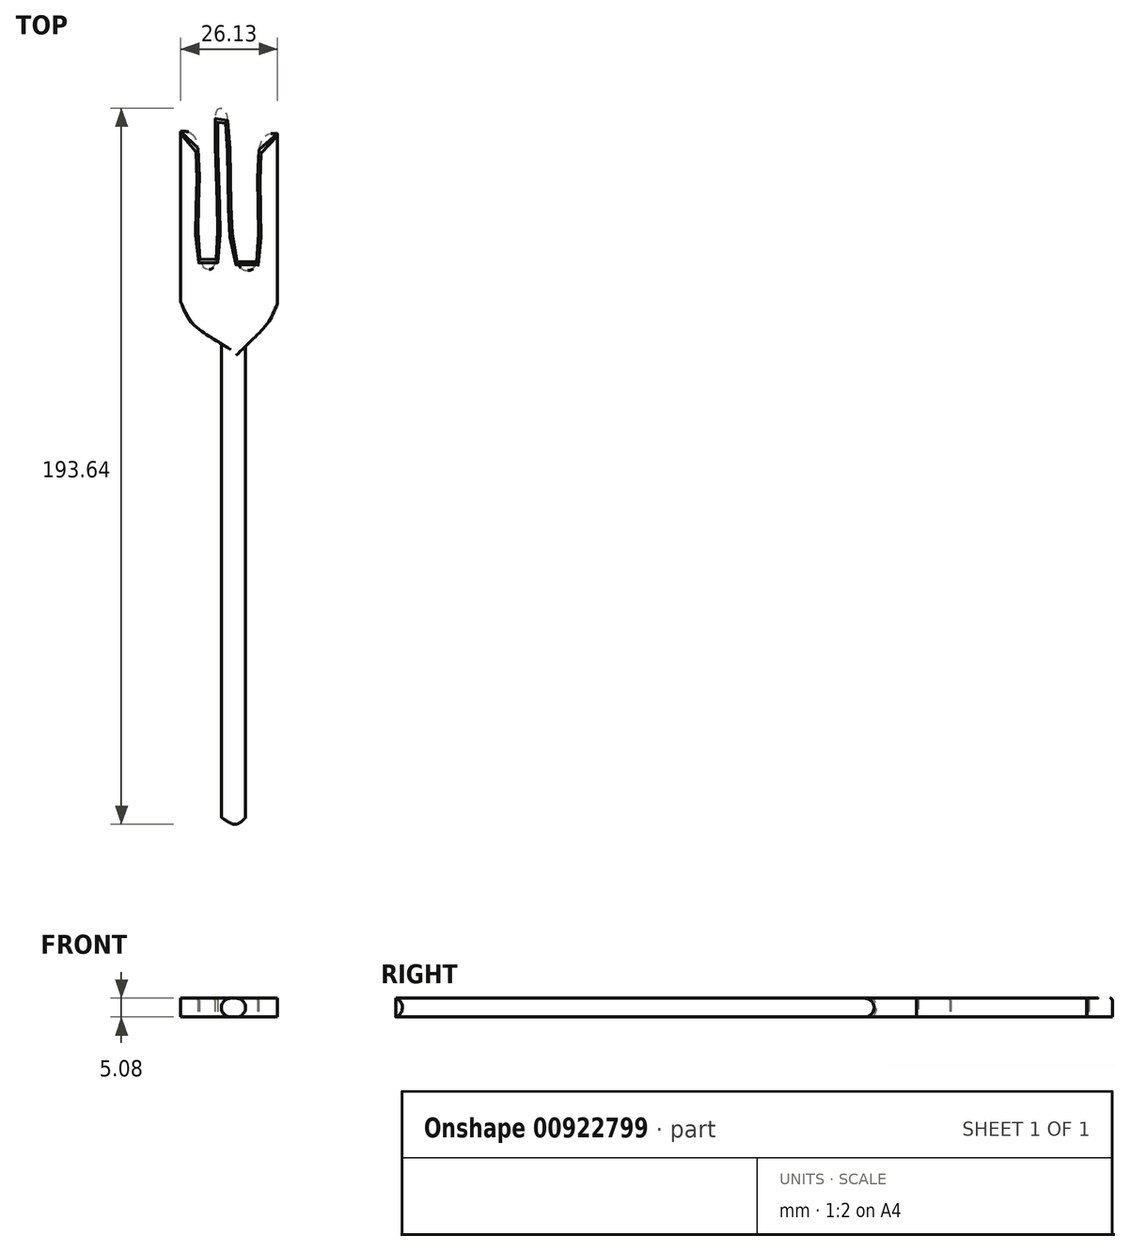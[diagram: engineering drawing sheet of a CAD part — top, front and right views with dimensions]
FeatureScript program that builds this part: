
annotation { "Feature Type Name" : "Feature", "Feature Type Description" : "" }
export const myFeature = defineFeature(function(context is Context, id is Id, definition is map)
    precondition{}
    {
        {
            var Q0;
            Q0=qCreatedBy(makeId("Top.planeOp"),FACE);
            var sketch = newSketch(context, id + "F0", { "sketchPlane" : qUnion([Q0])});
            skLineSegment(sketch, "E0", {"start": v(-28.75, 39.47) * mm, "end": v(-28.75, -87.53) * mm});
            skLineSegment(sketch, "E1", {"start": v(-17.13, 39.73) * mm, "end": v(-17.13, -87.27) * mm});
            skFitSpline(sketch, "E2", {"points": [v(-28.75, -87.53) * mm, v(-24.05, -91.53) * mm, v(-17.13, -87.27) * mm], "startDerivative": vector(9.45, -12.43) * mm, "endDerivative": vector(23.62, 29.9) * mm});
            skLineSegment(sketch, "E3", {"start": v(-37.2, 95.37) * mm, "end": v(-37.2, 49.28) * mm});
            skLineSegment(sketch, "E4", {"start": v(-11.06, 94.71) * mm, "end": v(-11.06, 48.78) * mm});
            skFitSpline(sketch, "E5", {"points": [v(-37.2, 49.28) * mm, v(-34.12, 43.55) * mm, v(-28.75, 39.47) * mm], "startDerivative": vector(5.1, -12.43) * mm, "endDerivative": vector(11.75, -7.22) * mm});
            skFitSpline(sketch, "E6", {"points": [v(-11.06, 48.78) * mm, v(-13.4, 43.91) * mm, v(-17.13, 39.73) * mm], "startDerivative": vector(-4.07, -10.2) * mm, "endDerivative": vector(-8.06, -7.9) * mm});
            skFitSpline(sketch, "E7", {"points": [v(-37.2, 95.37) * mm, v(-33.17, 93.3) * mm, v(-32.05, 61.08) * mm, v(-29.55, 58.02) * mm, v(-27.6, 60.52) * mm, v(-27.6, 100.25) * mm, v(-26.5, 101.64) * mm, v(-24.83, 99.97) * mm, v(-22.05, 60.24) * mm, v(-18.72, 57.74) * mm, v(-16.5, 60.52) * mm, v(-15.59, 92.05) * mm, v(-11.06, 94.71) * mm], "startDerivative": vector(87.16, -0.3) * mm, "endDerivative": vector(113.72, -13.53) * mm});
            skSolve(sketch);
        }
        {
            var Q0;
            Q0=makeQuery(id+"F0.imprint","IMPRINT",FACE,{"disambiguationData":[TD([[makeQuery(id+"F0.imprint","IMPRINT",EDGE,{"derivedFrom":sQuery(id+"F0.wireOp",EDGE,"E0")}),1.0]])]});
            extrude(context, id + "F1", {"entities" : qUnion([Q0]), "depth" : 5.08 * mm, "offsetDistance" : 25.4 * mm});
        }
        {
            var Q0;
            Q0=makeQuery(id+"F1.opExtrude","CAP_EDGE",EDGE,{"disambiguationData":[OSD([sQuery(id+"F0.wireOp",EDGE,"E7")])],"isStart":false});
            fillet(context, id + "F2", {"entities" : qUnion([Q0]), "radius" : 0.61 * mm, "tangentPropagation" : true, "allowEdgeOverflow" : false});
        }
        {
            var Q0;
            Q0=makeQuery(id+"F1.opExtrude","CAP_EDGE",EDGE,{"disambiguationData":[OSD([sQuery(id+"F0.wireOp",EDGE,"E0")])],"isStart":false});
            var Q1;
            Q1=makeQuery(id+"F1.opExtrude","CAP_EDGE",EDGE,{"disambiguationData":[OSD([sQuery(id+"F0.wireOp",EDGE,"E1")])],"isStart":false});
            fillet(context, id + "F3", {"entities" : qUnion([Q0, Q1]), "radius" : 5.08 * mm, "tangentPropagation" : true, "allowEdgeOverflow" : false});
        }
        {
            var Q0;
            {var subQ0=sQuery(id+"F0.wireOp",EDGE,"E1");Q0=makeQuery(id+"F3.opFillet","BLEND_EDGE",EDGE,{"blendedFrom":[makeQuery(id+"F1.opExtrude","CAP_EDGE",EDGE,{"disambiguationData":[OSD([subQ0])],"isStart":false}),makeQuery(id+"F1.opExtrude","CAP_FACE",FACE,{"disambiguationData":[OSD([sQuery(id+"F0.wireOp",EDGE,"E0"),subQ0,sQuery(id+"F0.wireOp",EDGE,"E2"),sQuery(id+"F0.wireOp",EDGE,"E3"),sQuery(id+"F0.wireOp",EDGE,"E4"),sQuery(id+"F0.wireOp",EDGE,"E5"),sQuery(id+"F0.wireOp",EDGE,"E6"),sQuery(id+"F0.wireOp",EDGE,"E7")])],"isStart":true})],"blendedInto":[makeQuery(id+"F1.opExtrude","CAP_FACE",FACE,{"disambiguationData":[OSD([sQuery(id+"F0.wireOp",EDGE,"E0"),subQ0,sQuery(id+"F0.wireOp",EDGE,"E2"),sQuery(id+"F0.wireOp",EDGE,"E3"),sQuery(id+"F0.wireOp",EDGE,"E4"),sQuery(id+"F0.wireOp",EDGE,"E5"),sQuery(id+"F0.wireOp",EDGE,"E6"),sQuery(id+"F0.wireOp",EDGE,"E7")])],"isStart":true})]});}
            var Q1;
            {var subQ0=sQuery(id+"F0.wireOp",EDGE,"E0");Q1=makeQuery(id+"F3.opFillet","BLEND_EDGE",EDGE,{"blendedFrom":[makeQuery(id+"F1.opExtrude","CAP_EDGE",EDGE,{"disambiguationData":[OSD([subQ0])],"isStart":false}),makeQuery(id+"F1.opExtrude","CAP_FACE",FACE,{"disambiguationData":[OSD([subQ0,sQuery(id+"F0.wireOp",EDGE,"E1"),sQuery(id+"F0.wireOp",EDGE,"E2"),sQuery(id+"F0.wireOp",EDGE,"E3"),sQuery(id+"F0.wireOp",EDGE,"E4"),sQuery(id+"F0.wireOp",EDGE,"E5"),sQuery(id+"F0.wireOp",EDGE,"E6"),sQuery(id+"F0.wireOp",EDGE,"E7")])],"isStart":true})],"blendedInto":[makeQuery(id+"F1.opExtrude","CAP_FACE",FACE,{"disambiguationData":[OSD([subQ0,sQuery(id+"F0.wireOp",EDGE,"E1"),sQuery(id+"F0.wireOp",EDGE,"E2"),sQuery(id+"F0.wireOp",EDGE,"E3"),sQuery(id+"F0.wireOp",EDGE,"E4"),sQuery(id+"F0.wireOp",EDGE,"E5"),sQuery(id+"F0.wireOp",EDGE,"E6"),sQuery(id+"F0.wireOp",EDGE,"E7")])],"isStart":true})]});}
            fillet(context, id + "F4", {"entities" : qUnion([Q0, Q1]), "radius" : 2.54 * mm, "tangentPropagation" : true, "allowEdgeOverflow" : false});
        }
    });
